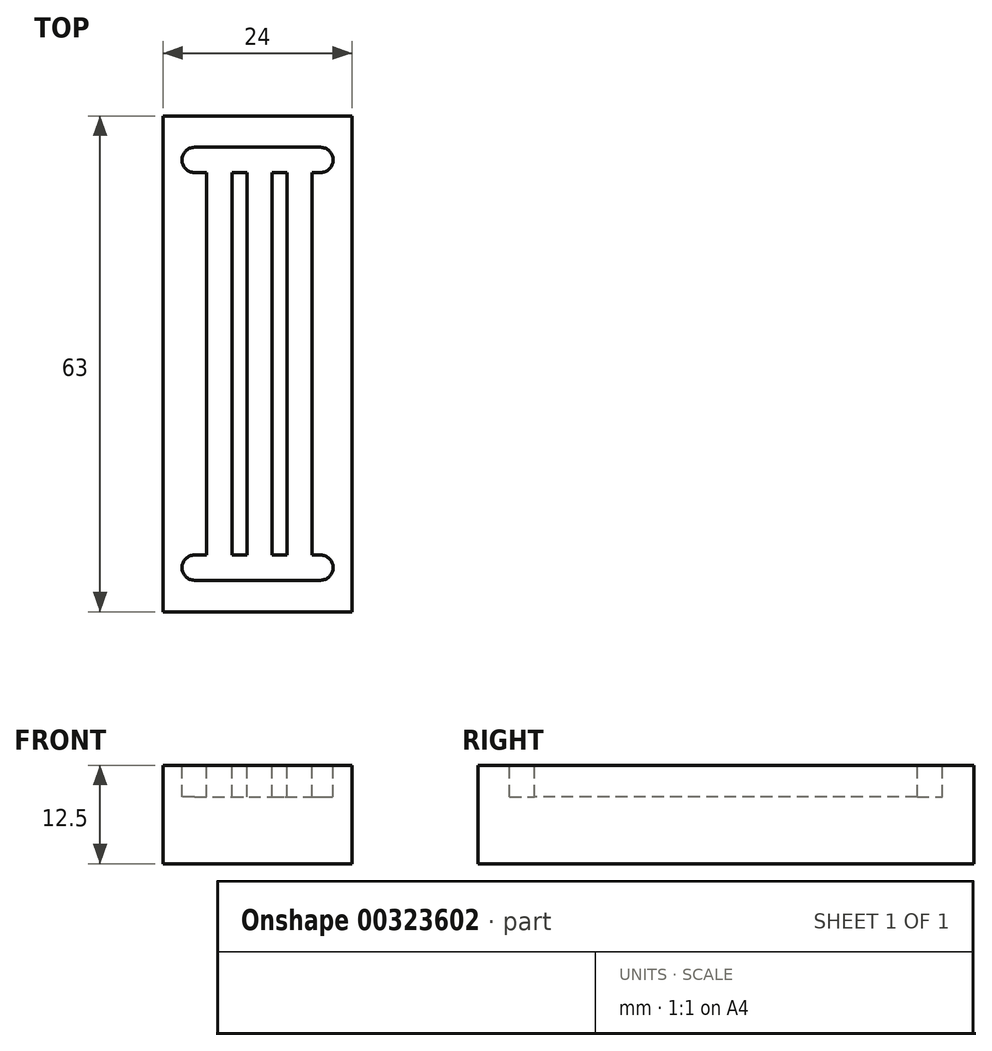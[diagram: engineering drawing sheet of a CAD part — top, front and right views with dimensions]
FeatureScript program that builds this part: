
annotation { "Feature Type Name" : "Feature", "Feature Type Description" : "" }
export const myFeature = defineFeature(function(context is Context, id is Id, definition is map)
    precondition{}
    {
        {
            var Q0;
            Q0=qCreatedBy(makeId("Top.planeOp"),FACE);
            var sketch = newSketch(context, id + "F0", { "sketchPlane" : qUnion([Q0])});
            skLineSegment(sketch, "E0.bottom", {"start": v(0, 0) * mm, "end": v(24, 0) * mm});
            skLineSegment(sketch, "E0.top", {"start": v(0, 63) * mm, "end": v(24, 63) * mm});
            skLineSegment(sketch, "E0.left", {"start": v(0, 0) * mm, "end": v(0, 63) * mm});
            skLineSegment(sketch, "E0.right", {"start": v(24, 0) * mm, "end": v(24, 63) * mm});
            skSolve(sketch);
        }
        {
            var Q0;
            Q0 = qSketchRegion(id + "F0", true);
            extrude(context, id + "F1", {"entities" : qUnion([Q0]), "depth" : 12.5 * mm});
        }
        {
            var Q0;
            Q0=makeQuery(id+"F1.opExtrude","CAP_FACE",FACE,{"disambiguationData":[OSD([sQuery(id+"F0.wireOp",EDGE,"E0.bottom"),sQuery(id+"F0.wireOp",EDGE,"E0.top"),sQuery(id+"F0.wireOp",EDGE,"E0.left"),sQuery(id+"F0.wireOp",EDGE,"E0.right")])],"isStart":false});
            var sketch = newSketch(context, id + "F2", { "sketchPlane" : qUnion([Q0])});
            skLineSegment(sketch, "E1.bottom", {"start": v(5.55, 59) * mm, "end": v(8.75, 59) * mm});
            skLineSegment(sketch, "E1.top", {"start": v(5.55, 4) * mm, "end": v(8.75, 4) * mm});
            skLineSegment(sketch, "E1.left", {"start": v(5.55, 59) * mm, "end": v(5.55, 4) * mm});
            skLineSegment(sketch, "E1.right", {"start": v(8.75, 59) * mm, "end": v(8.75, 4) * mm});
            skLineSegment(sketch, "E2.bottom", {"start": v(13.85, 59) * mm, "end": v(10.65, 59) * mm});
            skLineSegment(sketch, "E2.top", {"start": v(13.85, 4) * mm, "end": v(10.65, 4) * mm});
            skLineSegment(sketch, "E2.left", {"start": v(13.85, 59) * mm, "end": v(13.85, 4) * mm});
            skLineSegment(sketch, "E2.right", {"start": v(10.65, 59) * mm, "end": v(10.65, 4) * mm});
            skLineSegment(sketch, "E3.bottom", {"start": v(15.75, 59) * mm, "end": v(18.95, 59) * mm});
            skLineSegment(sketch, "E3.top", {"start": v(15.75, 4) * mm, "end": v(18.95, 4) * mm});
            skLineSegment(sketch, "E3.left", {"start": v(15.75, 59) * mm, "end": v(15.75, 4) * mm});
            skLineSegment(sketch, "E3.right", {"start": v(18.95, 59) * mm, "end": v(18.95, 4) * mm});
            skSolve(sketch);
        }
        {
            var Q0;
            Q0 = qSketchRegion(id + "F2", true);
            extrude(context, id + "F3", {"entities" : qUnion([Q0]), "operationType" : NewBodyOperationType.REMOVE, "oppositeDirection" : true, "depth" : 4 * mm});
        }
        {
            var Q0;
            Q0=makeQuery(id+"F1.opExtrude","CAP_FACE",FACE,{"disambiguationData":[OSD([sQuery(id+"F0.wireOp",EDGE,"E0.bottom"),sQuery(id+"F0.wireOp",EDGE,"E0.top"),sQuery(id+"F0.wireOp",EDGE,"E0.left"),sQuery(id+"F0.wireOp",EDGE,"E0.right")])],"isStart":false});
            var sketch = newSketch(context, id + "F4", { "sketchPlane" : qUnion([Q0])});
            skLineSegment(sketch, "E4.bottom", {"start": v(4, 59) * mm, "end": v(20, 59) * mm});
            skLineSegment(sketch, "E4.top", {"start": v(4, 55.8) * mm, "end": v(20, 55.8) * mm});
            skLineSegment(sketch, "E4.left", {"start": v(4, 59) * mm, "end": v(4, 55.8) * mm});
            skLineSegment(sketch, "E4.right", {"start": v(20, 59) * mm, "end": v(20, 55.8) * mm});
            skLineSegment(sketch, "E5.bottom", {"start": v(4, 4) * mm, "end": v(20, 4) * mm});
            skLineSegment(sketch, "E5.top", {"start": v(4, 7.2) * mm, "end": v(20, 7.2) * mm});
            skLineSegment(sketch, "E5.left", {"start": v(4, 4) * mm, "end": v(4, 7.2) * mm});
            skLineSegment(sketch, "E5.right", {"start": v(20, 4) * mm, "end": v(20, 7.2) * mm});
            skArc(sketch, "E6", {"start": v(20, 55.8) * mm, "mid": v(21.6, 57.4) * mm, "end": v(20, 59) * mm});
            skArc(sketch, "E7", {"start": v(4, 59) * mm, "mid": v(2.4, 57.4) * mm, "end": v(4, 55.8) * mm});
            skArc(sketch, "E8", {"start": v(20, 4) * mm, "mid": v(21.6, 5.6) * mm, "end": v(20, 7.2) * mm});
            skArc(sketch, "E9", {"start": v(4, 7.2) * mm, "mid": v(2.4, 5.6) * mm, "end": v(4, 4) * mm});
            skSolve(sketch);
        }
        {
            var Q0;
            Q0 = qSketchRegion(id + "F4", true);
            extrude(context, id + "F5", {"entities" : qUnion([Q0]), "operationType" : NewBodyOperationType.REMOVE, "oppositeDirection" : true, "depth" : 4 * mm});
        }
    });
